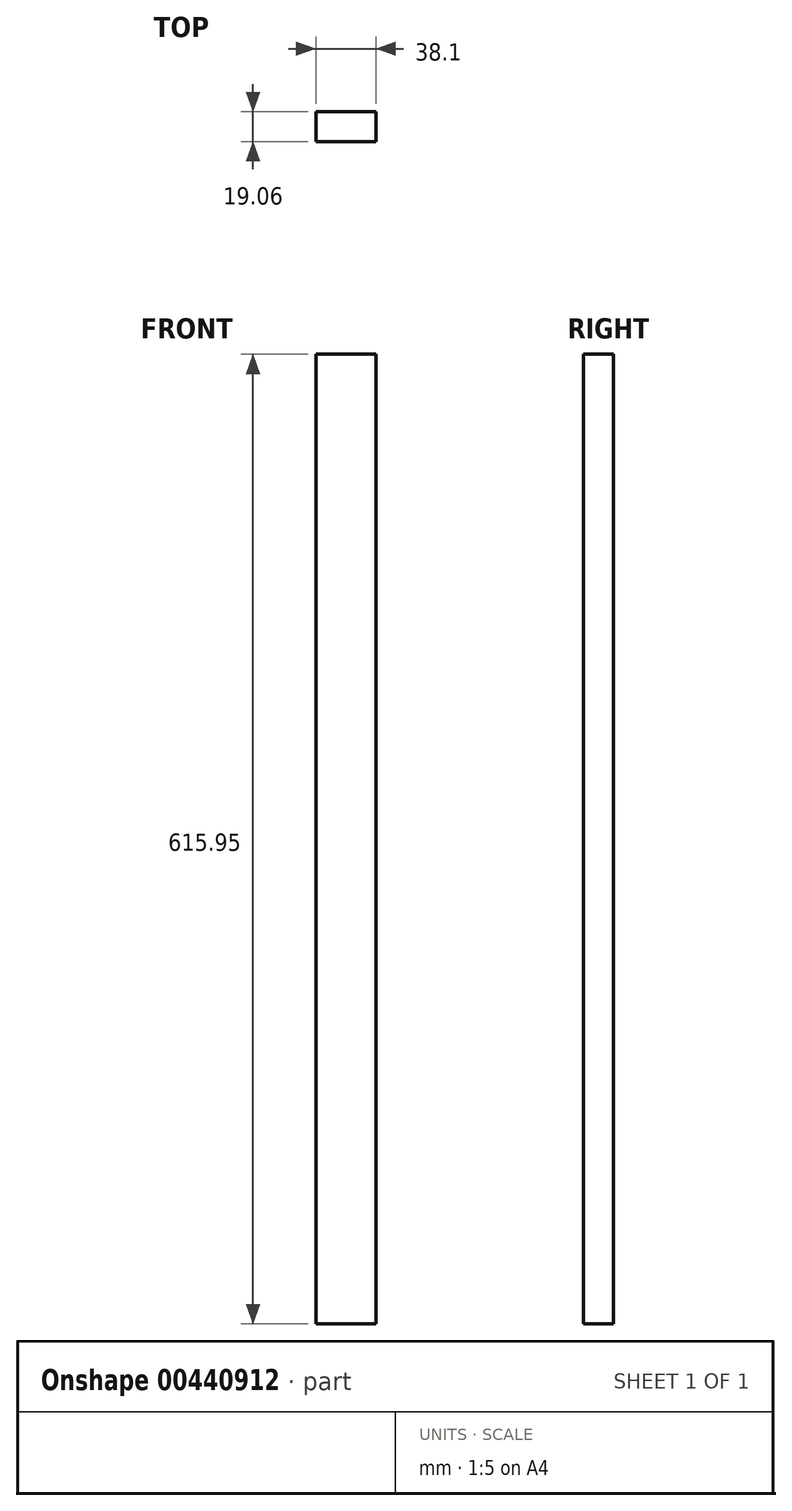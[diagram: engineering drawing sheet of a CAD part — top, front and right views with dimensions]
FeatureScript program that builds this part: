
annotation { "Feature Type Name" : "Feature", "Feature Type Description" : "" }
export const myFeature = defineFeature(function(context is Context, id is Id, definition is map)
    precondition{}
    {
        {
            var Q0;
            Q0=qCreatedBy(makeId("Top.planeOp"),FACE);
            var sketch = newSketch(context, id + "F0", { "sketchPlane" : qUnion([Q0])});
            skLineSegment(sketch, "E0.bottom", {"start": v(19.05, 9.53) * mm, "end": v(-19.05, 9.53) * mm});
            skLineSegment(sketch, "E0.top", {"start": v(19.05, -9.53) * mm, "end": v(-19.05, -9.53) * mm});
            skLineSegment(sketch, "E0.left", {"start": v(19.05, 9.52) * mm, "end": v(19.05, -9.53) * mm});
            skLineSegment(sketch, "E0.right", {"start": v(-19.05, 9.53) * mm, "end": v(-19.05, -9.53) * mm});
            skPoint(sketch, "E0.middle", {"position": v(0, 0) * mm});
            skSolve(sketch);
        }
        {
            var Q0;
            Q0 = qSketchRegion(id + "F0", true);
            extrude(context, id + "F1", {"entities" : qUnion([Q0]), "depth" : 615.95 * mm});
        }
    });
